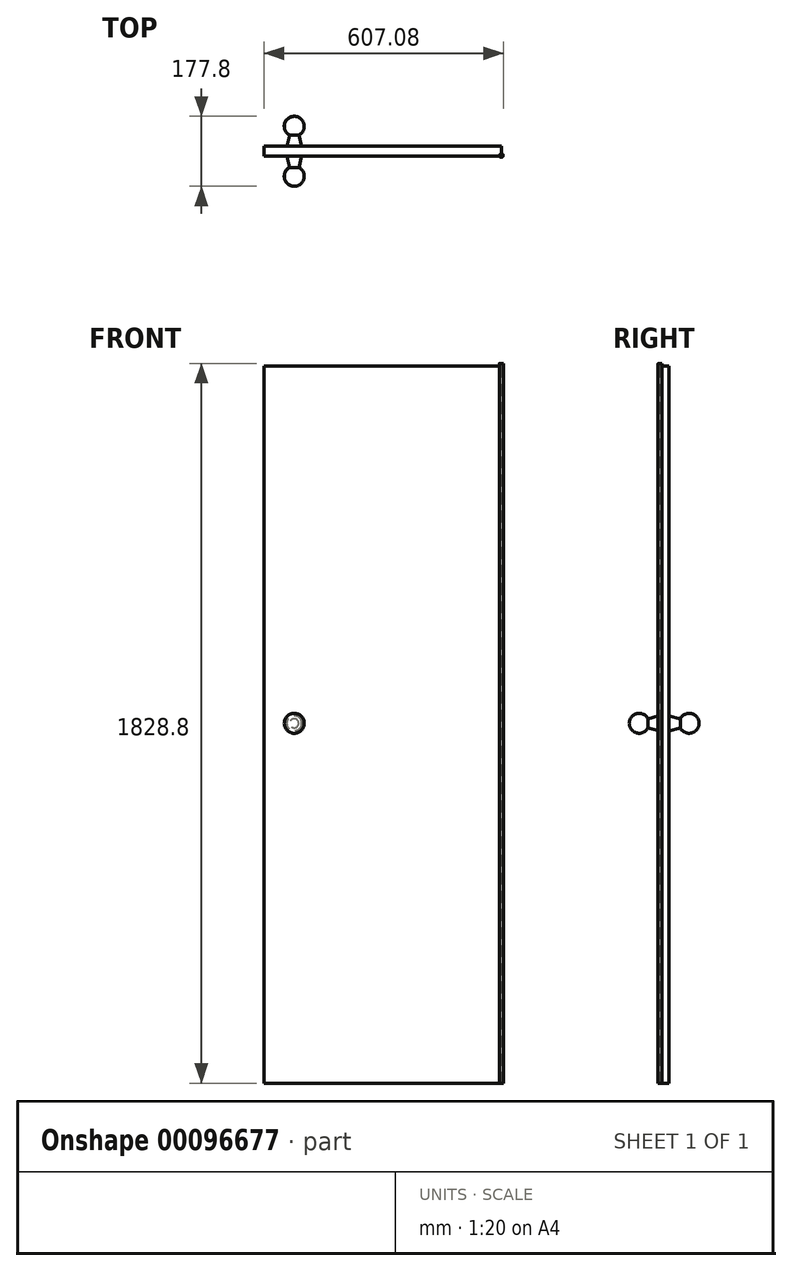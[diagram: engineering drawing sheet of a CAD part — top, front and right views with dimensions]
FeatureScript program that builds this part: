
annotation { "Feature Type Name" : "Feature", "Feature Type Description" : "" }
export const myFeature = defineFeature(function(context is Context, id is Id, definition is map)
    precondition{}
    {
        {
            var Q0;
            Q0=qCreatedBy(makeId("Front.planeOp"),FACE);
            var sketch = newSketch(context, id + "F0", { "sketchPlane" : qUnion([Q0])});
            skLineSegment(sketch, "E0.bottom", {"start": v(0, 0) * mm, "end": v(603.25, 0) * mm});
            skLineSegment(sketch, "E0.top", {"start": v(0, 1822.45) * mm, "end": v(603.25, 1822.45) * mm});
            skLineSegment(sketch, "E0.left", {"start": v(0, 0) * mm, "end": v(0, 1822.45) * mm});
            skLineSegment(sketch, "E0.right", {"start": v(603.25, 0) * mm, "end": v(603.25, 1822.45) * mm});
            skLineSegment(sketch, "E1", {"start": v(-183.2, 914.4) * mm, "end": v(165.94, 914.4) * mm});
            skLineSegment(sketch, "E2", {"start": v(76.2, 1062.27) * mm, "end": v(76.2, 800.41) * mm});
            skCircle(sketch, "E3", {"center": v(76.2, 914.4) * mm, "radius": 73.32 * mm, "construction": true});
            skSolve(sketch);
        }
        {
            var Q0;
            Q0 = qSketchRegion(id + "F0", true);
            extrude(context, id + "F1", {"entities" : qUnion([Q0]), "depth" : 25.4 * mm});
        }
        {
            var Q0;
            Q0=qCreatedBy(makeId("Top.planeOp"),FACE);
            cPlane(context, id + "F2", {"entities" : qUnion([Q0]), "cplaneType" : CPlaneType.OFFSET, "offset" : 914.4 * mm, "width" : 152.4 * mm, "height" : 152.4 * mm});
        }
        {
            var Q0;
            Q0=qCreatedBy(id+"F2.planeOp",FACE);
            var sketch = newSketch(context, id + "F3", { "sketchPlane" : qUnion([Q0])});
            skArc(sketch, "E4", {"start": v(64.7, -53.56) * mm, "mid": v(51.5, -82.12) * mm, "end": v(76.2, -101.6) * mm});
            skLineSegment(sketch, "E5", {"start": v(57.15, -25.4) * mm, "end": v(64.7, -53.56) * mm});
            skLineSegment(sketch, "E6", {"start": v(76.2, -25.4) * mm, "end": v(57.15, -25.4) * mm});
            skLineSegment(sketch, "E7", {"start": v(76.2, -25.4) * mm, "end": v(76.2, -101.6) * mm});
            skSolve(sketch);
        }
        {
            var Q0;
            Q0=makeQuery(id+"F1.opExtrude","CAP_FACE",FACE,{"disambiguationData":[OSD([sQuery(id+"F0.wireOp",EDGE,"E0.bottom"),sQuery(id+"F0.wireOp",EDGE,"E0.top"),sQuery(id+"F0.wireOp",EDGE,"E0.left"),sQuery(id+"F0.wireOp",EDGE,"E0.right")])],"isStart":false});
            var sketch = newSketch(context, id + "F4", { "sketchPlane" : qUnion([Q0])});
            skCircle(sketch, "E8", {"center": v(76.2, 914.4) * mm, "radius": 21.63 * mm});
            skSolve(sketch);
        }
        {
            var Q0;
            Q0=makeQuery(id+"F3.imprint","IMPRINT",FACE,{"disambiguationData":[TD([[makeQuery(id+"F3.imprint","IMPRINT",EDGE,{"derivedFrom":sQuery(id+"F3.wireOp",EDGE,"E4")}),1.0]])]});
            var Q1;
            Q1=sQuery(id+"F4.wireOp",EDGE,"E8");
            sweep(context, id + "F5", {"profiles" : qUnion([Q0]), "path" : qUnion([Q1])});
        }
        {
            var Q0;
            Q0=qCreatedBy(makeId("Front.planeOp"),FACE);
            cPlane(context, id + "F6", {"entities" : qUnion([Q0]), "cplaneType" : CPlaneType.OFFSET, "offset" : 12.7 * mm, "width" : 152.4 * mm, "height" : 152.4 * mm});
        }
        {
            var Q0;
            Q0=makeQuery(id+"F5.opSweep","SWEPT_BODY",BODY,{"disambiguationData":[OSD([sQuery(id+"F3.wireOp",EDGE,"E4"),sQuery(id+"F3.wireOp",EDGE,"E5"),sQuery(id+"F3.wireOp",EDGE,"E6"),sQuery(id+"F3.wireOp",EDGE,"E7"),sQuery(id+"F4.wireOp",EDGE,"E8")])]});
            var Q1;
            Q1=qCreatedBy(id+"F6.planeOp",FACE);
            mirror(context, id + "F7", {"operationType" : NewBodyOperationType.ADD, "entities" : qUnion([Q0]), "mirrorPlane" : qUnion([Q1])});
        }
        {
            var Q0;
            Q0=qCreatedBy(makeId("Top.planeOp"),FACE);
            var sketch = newSketch(context, id + "F8", { "sketchPlane" : qUnion([Q0])});
            skCircle(sketch, "E9", {"center": v(602.32, -23.37) * mm, "radius": 4.76 * mm});
            skSolve(sketch);
        }
        {
            var Q0;
            Q0 = qSketchRegion(id + "F8", true);
            extrude(context, id + "F9", {"entities" : qUnion([Q0]), "operationType" : NewBodyOperationType.ADD, "depth" : 1828.8 * mm});
        }
    });
